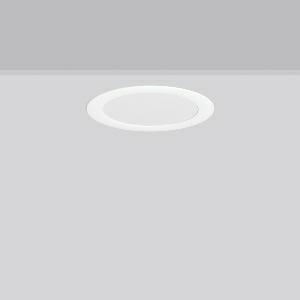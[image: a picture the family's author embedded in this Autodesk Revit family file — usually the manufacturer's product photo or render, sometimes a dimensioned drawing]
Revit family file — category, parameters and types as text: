
# Revit family: toledo_flat_round_e_901715_002_1_19_9782
name_source: partatom
category: Lighting Fixtures
units: mm (PartAtom-declared; Revit-internal decimal feet)

## family parameters
Cut with Voids When Loaded = No
Host = Face
Light Source = No
Part Type = Normal
Room Calculation Point = No
Round Connector Dimension = Use Diameter
Shared = No

## types (1)
- TOLEDO FLAT round E (1 x LED Modul 840, 1800 lm, 4000)
    Apparent Load = 17 VA
    CIE Flux Codes = 48 79 96 100 100
    Color Rendering = 80
    Color Temperature = 4000
    Default Elevation = 1800 mm  [stored 5.90551 ft]
    Description = Series: TOLEDO FLAT round
Ultra thin recessed downlight. Housing: die-cast aluminium. Light guide and diffuser made of non-yellowing PMMA, opal matt. Ceiling installation with spring system. Mounting depth depends on ceiling strength. Including separate LED converter with connecting cable 250 mm.Connected HF motion detector in a separate ballast box. Adjustable dim functions Soft Start, Corridor, Permanent. Wireless networking, sensor configuration and communication via Bluetooth. Operation via an Android / iOS device, free app available for download. master/slave Brightness sensor without function. Not suitable for metal ceilings.Versions with movement sensor not suitable for surface-mounted housing. Suitable for through-wiring with separately available accessories. Retrofittable decorative cylinders made of chintz fabric as accessory, optional with satin finish plastic diffuser. Through-wiring box (5 pole) available as accessory. 
Colour: white
Diameter: 255 mm
Height: 3 mm
Cut-out diameter: 234 mm
Recess height: 55-76 mm
Luminaire: recess height: 31-51 mm
Lamp: LED
Socket: without socket
Colour temperature: 4000K
Colour rendering index (CRI): 80
System power: 17 W
Rated luminous flux: 1800 lm
Luminous efficiency: 106 lm/W
Control gear: Dimmable Bluetooth converter
Protection class: I
Type of protection: IP 54
    Height = 0 mm  [stored 0 ft]
    Lamp = 1 x LED Modul 840
    Lamp Light Flux = 1800 lm
    Lamp count = 1
    Length = 255 mm
    Lifetime = 50000 h
    Luminous efficacy = 106 lm/W
    Manufacturer = RZB
    ModVariant = No
    Model = 901715.002.1.19
    Mounting Place = Ceiling
    Mounting Type = Recessed
    Number of Poles = 1
    OnlyDefault = Yes
    Power Factor = 1
    Product Name = TOLEDO FLAT round E
    Product group = Recessed downlights
    ProductGroupID = 402
    Protection Class = Protection class I
    Protection Degree = IP 20
    RLX_Detail_Level = 1
    RLX_Emergency_Light_Flux = 0 lm
    RLX_Emergency_Type = 0
    RLX_Emergency_Type_DB = No
    RlxData = <blob elided: 30605 chars, md5=3fa62b3f>
    Socket = socket
    Standby Power = 0 W
    System Light Flux = 1800 lm
    System Power = 17 W
    Type Comments = Product without accessories
    Type Image = 901453.002.jpg
    URL = http://relux.com
    VarID = ---
    Voltage = 230 V
    Voltage Range = 220-240 V
    Weight = 0.00 kg
    Width = 0 mm  [stored 0 ft]

note: [stored X ft] marks values corroborated as IEEE doubles in the binary element streams (Revit-internal decimal feet)

## geometry (parser evidence)
native form markers: Blend x4, Sweep x12
no freeform markers — native parametric forms only
